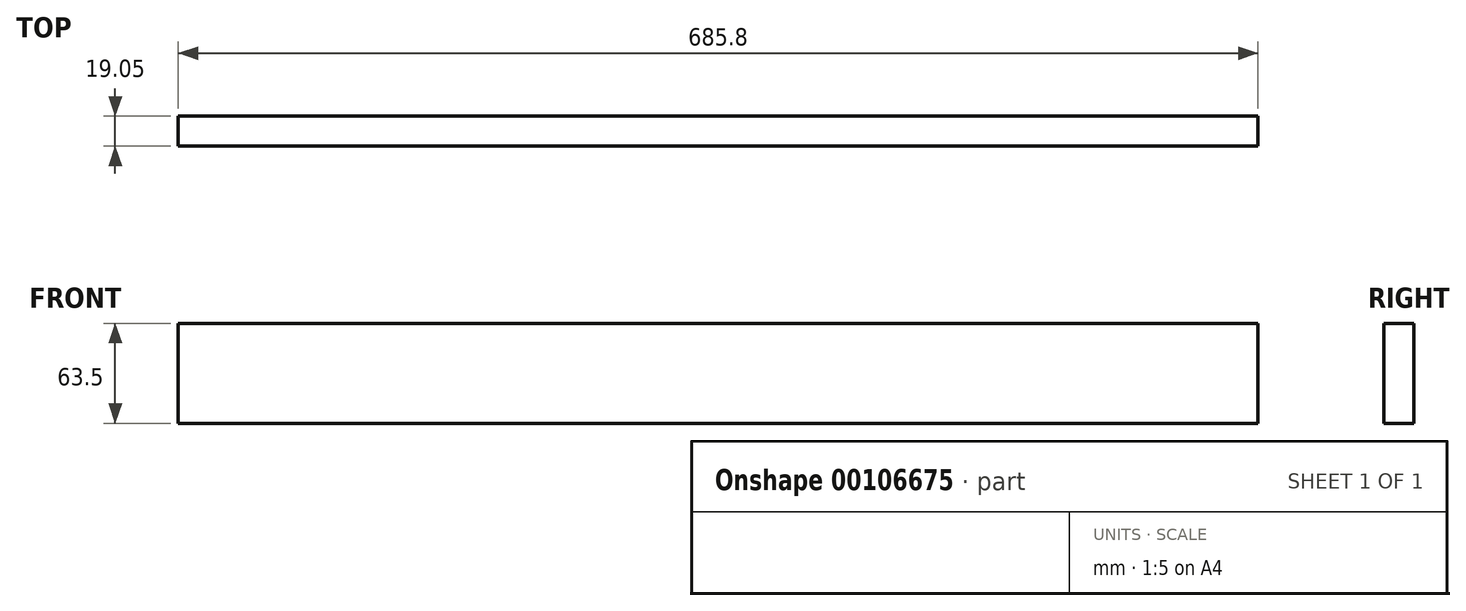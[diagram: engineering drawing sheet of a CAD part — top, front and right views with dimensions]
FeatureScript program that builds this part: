
annotation { "Feature Type Name" : "Feature", "Feature Type Description" : "" }
export const myFeature = defineFeature(function(context is Context, id is Id, definition is map)
    precondition{}
    {
        {
            var Q0;
            Q0=qCreatedBy(makeId("Front.planeOp"),FACE);
            var sketch = newSketch(context, id + "F0", { "sketchPlane" : qUnion([Q0])});
            skLineSegment(sketch, "E0.bottom", {"start": v(0, 0) * mm, "end": v(685.8, 0) * mm});
            skLineSegment(sketch, "E0.top", {"start": v(0, 63.5) * mm, "end": v(685.8, 63.5) * mm});
            skLineSegment(sketch, "E0.left", {"start": v(0, 0) * mm, "end": v(0, 63.5) * mm});
            skLineSegment(sketch, "E0.right", {"start": v(685.8, 0) * mm, "end": v(685.8, 63.5) * mm});
            skSolve(sketch);
        }
        {
            var Q0;
            Q0=makeQuery(id+"F0.imprint","IMPRINT",FACE,{"disambiguationData":[TD([[makeQuery(id+"F0.imprint","IMPRINT",EDGE,{"derivedFrom":sQuery(id+"F0.wireOp",EDGE,"E0.bottom")}),1.0]])]});
            extrude(context, id + "F1", {"entities" : qUnion([Q0]), "depth" : 19.05 * mm});
        }
    });
